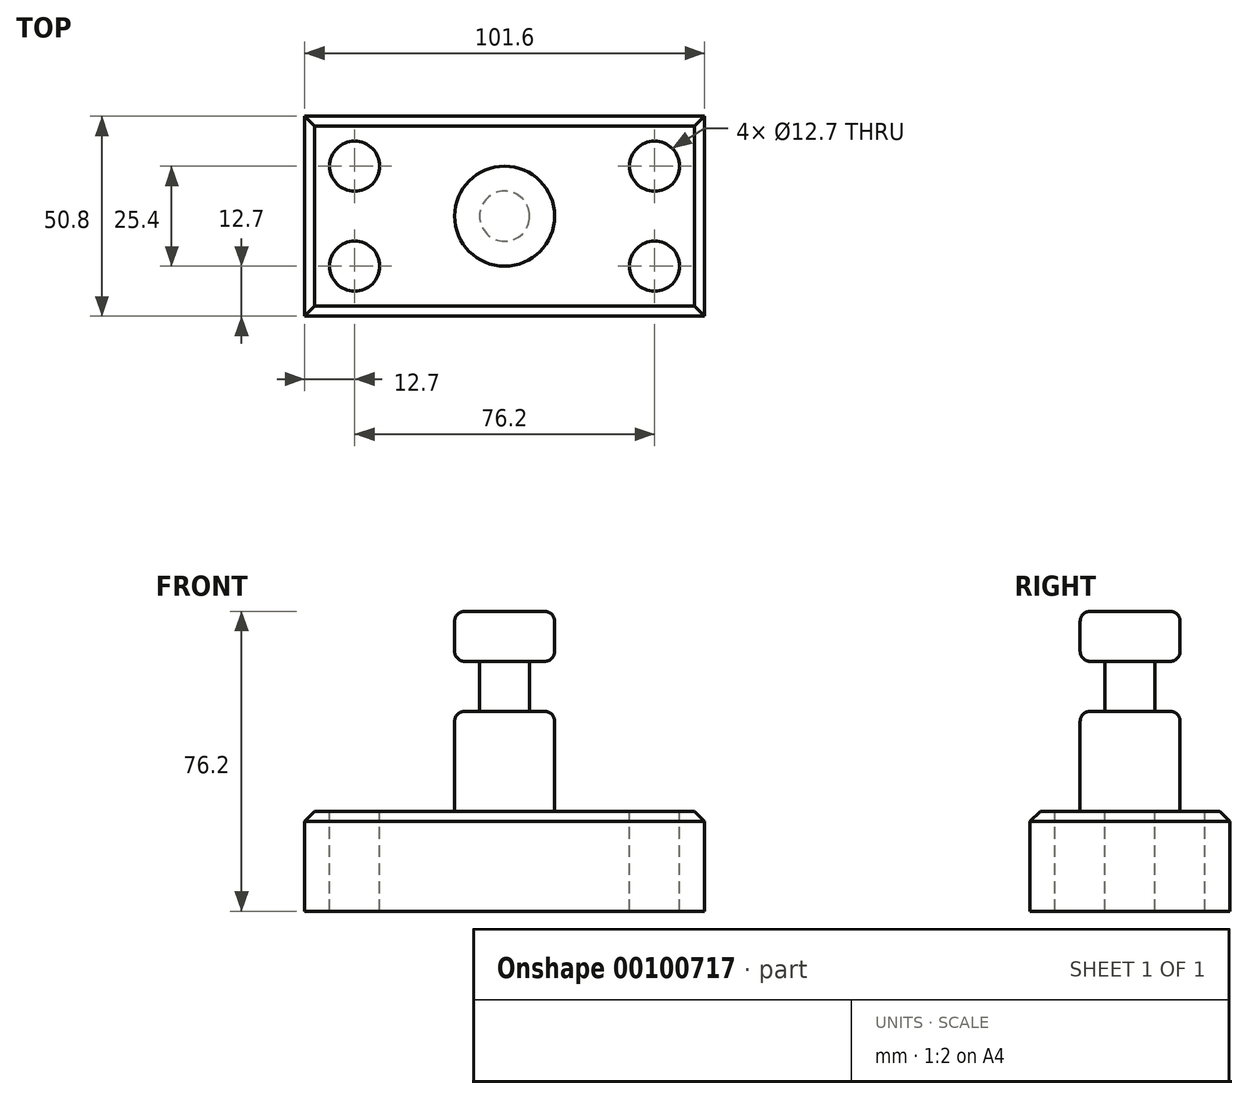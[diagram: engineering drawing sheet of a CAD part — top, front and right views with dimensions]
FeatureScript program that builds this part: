
annotation { "Feature Type Name" : "Feature", "Feature Type Description" : "" }
export const myFeature = defineFeature(function(context is Context, id is Id, definition is map)
    precondition{}
    {
        {
            var Q0;
            Q0=qCreatedBy(makeId("Top.planeOp"),FACE);
            var sketch = newSketch(context, id + "F0", { "sketchPlane" : qUnion([Q0])});
            skLineSegment(sketch, "E0.bottom", {"start": v(-50.8, 25.4) * mm, "end": v(50.8, 25.4) * mm});
            skLineSegment(sketch, "E0.top", {"start": v(-50.8, -25.4) * mm, "end": v(50.8, -25.4) * mm});
            skLineSegment(sketch, "E0.left", {"start": v(-50.8, 25.4) * mm, "end": v(-50.8, -25.4) * mm});
            skLineSegment(sketch, "E0.right", {"start": v(50.8, 25.4) * mm, "end": v(50.8, -25.4) * mm});
            skPoint(sketch, "E0.middle", {"position": v(0, 0) * mm});
            skSolve(sketch);
        }
        {
            var Q0;
            Q0 = qSketchRegion(id + "F0", true);
            extrude(context, id + "F1", {"entities" : qUnion([Q0]), "depth" : 25.4 * mm});
        }
        {
            var Q0;
            Q0=makeQuery(id+"F1.opExtrude","CAP_FACE",FACE,{"disambiguationData":[OSD([sQuery(id+"F0.wireOp",EDGE,"E0.bottom"),sQuery(id+"F0.wireOp",EDGE,"E0.top"),sQuery(id+"F0.wireOp",EDGE,"E0.left"),sQuery(id+"F0.wireOp",EDGE,"E0.right")])],"isStart":false});
            var sketch = newSketch(context, id + "F2", { "sketchPlane" : qUnion([Q0])});
            skCircle(sketch, "E1", {"center": v(-38.1, 12.7) * mm, "radius": 6.35 * mm});
            skCircle(sketch, "E2", {"center": v(38.1, 12.7) * mm, "radius": 6.35 * mm});
            skCircle(sketch, "E3", {"center": v(38.1, -12.7) * mm, "radius": 6.35 * mm});
            skCircle(sketch, "E4", {"center": v(-38.1, -12.7) * mm, "radius": 6.35 * mm});
            skSolve(sketch);
        }
        {
            var Q0;
            Q0=makeQuery(id+"F2.imprint","IMPRINT",FACE,{"disambiguationData":[TD([[makeQuery(id+"F2.imprint","IMPRINT",EDGE,{"derivedFrom":sQuery(id+"F2.wireOp",EDGE,"E2")}),1.0]])]});
            var Q1;
            Q1=makeQuery(id+"F2.imprint","IMPRINT",FACE,{"disambiguationData":[TD([[makeQuery(id+"F2.imprint","IMPRINT",EDGE,{"derivedFrom":sQuery(id+"F2.wireOp",EDGE,"E1")}),1.0]])]});
            var Q2;
            Q2=makeQuery(id+"F2.imprint","IMPRINT",FACE,{"disambiguationData":[TD([[makeQuery(id+"F2.imprint","IMPRINT",EDGE,{"derivedFrom":sQuery(id+"F2.wireOp",EDGE,"E4")}),1.0]])]});
            var Q3;
            Q3=makeQuery(id+"F2.imprint","IMPRINT",FACE,{"disambiguationData":[TD([[makeQuery(id+"F2.imprint","IMPRINT",EDGE,{"derivedFrom":sQuery(id+"F2.wireOp",EDGE,"E3")}),1.0]])]});
            extrude(context, id + "F3", {"entities" : qUnion([Q0, Q1, Q2, Q3]), "operationType" : NewBodyOperationType.REMOVE, "endBound" : BoundingType.THROUGH_ALL, "oppositeDirection" : true, "depth" : 25.4 * mm});
        }
        {
            var Q0;
            Q0=qCreatedBy(makeId("Front.planeOp"),FACE);
            var sketch = newSketch(context, id + "F4", { "sketchPlane" : qUnion([Q0])});
            skLineSegment(sketch, "E5.bottom", {"start": v(0, 25.4) * mm, "end": v(-12.7, 25.4) * mm});
            skLineSegment(sketch, "E5.top", {"start": v(0, 76.2) * mm, "end": v(-12.7, 76.2) * mm});
            skLineSegment(sketch, "E5.left", {"start": v(0, 25.4) * mm, "end": v(0, 76.2) * mm});
            skLineSegment(sketch, "E5.right", {"start": v(-12.7, 25.4) * mm, "end": v(-12.7, 76.2) * mm});
            skSolve(sketch);
        }
        {
            var Q0;
            Q0 = qSketchRegion(id + "F4", true);
            var Q1;
            Q1=sQuery(id+"F4.wireOp",EDGE,"E5.left");
            revolve(context, id + "F5", {"operationType" : NewBodyOperationType.ADD, "entities" : qUnion([Q0]), "axis" : qUnion([Q1]), "revolveType" : RevolveType.FULL});
        }
        {
            var Q0;
            Q0=qCreatedBy(makeId("Front.planeOp"),FACE);
            var sketch = newSketch(context, id + "F6", { "sketchPlane" : qUnion([Q0])});
            skLineSegment(sketch, "E6.bottom", {"start": v(-19.05, 63.5) * mm, "end": v(-6.35, 63.5) * mm});
            skLineSegment(sketch, "E6.top", {"start": v(-19.05, 50.8) * mm, "end": v(-6.35, 50.8) * mm});
            skLineSegment(sketch, "E6.left", {"start": v(-19.05, 63.5) * mm, "end": v(-19.05, 50.8) * mm});
            skLineSegment(sketch, "E6.right", {"start": v(-6.35, 63.5) * mm, "end": v(-6.35, 50.8) * mm});
            skLineSegment(sketch, "E7", {"start": v(0, 0) * mm, "end": v(0, 81.72) * mm, "construction": true});
            skSolve(sketch);
        }
        {
            var Q0;
            Q0=makeQuery(id+"F6.imprint","IMPRINT",FACE,{"disambiguationData":[TD([[makeQuery(id+"F6.imprint","IMPRINT",EDGE,{"derivedFrom":sQuery(id+"F6.wireOp",EDGE,"E6.bottom")}),-1.0]])]});
            var Q1;
            Q1=sQuery(id+"F6.wireOp",EDGE,"E7");
            revolve(context, id + "F7", {"operationType" : NewBodyOperationType.REMOVE, "entities" : qUnion([Q0]), "axis" : qUnion([Q1]), "revolveType" : RevolveType.FULL, "oppositeDirection" : true});
        }
        {
            var Q0;
            Q0=makeQuery(id+"F7.boolean.opBoolean","INTERSECT",EDGE,{"derivedFrom":[makeQuery(id+"F5.opRevolve","SWEPT_FACE",FACE,{"disambiguationData":[OSD([sQuery(id+"F4.wireOp",EDGE,"E5.right")])]}),makeQuery(id+"F7.opRevolve","SWEPT_FACE",FACE,{"disambiguationData":[OSD([sQuery(id+"F6.wireOp",EDGE,"E6.top")])]})]});
            var Q1;
            Q1=makeQuery(id+"F7.boolean.opBoolean","INTERSECT",EDGE,{"derivedFrom":[makeQuery(id+"F5.opRevolve","SWEPT_FACE",FACE,{"disambiguationData":[OSD([sQuery(id+"F4.wireOp",EDGE,"E5.right")])]}),makeQuery(id+"F7.opRevolve","SWEPT_FACE",FACE,{"disambiguationData":[OSD([sQuery(id+"F6.wireOp",EDGE,"E6.bottom")])]})]});
            var Q2;
            Q2=makeQuery(id+"F5.opRevolve","SWEPT_EDGE",EDGE,{"disambiguationData":[OSD([sQuery(id+"F4.wireOp",EDGE,"E5.bottom"),sQuery(id+"F4.wireOp",EDGE,"E5.right")])]});
            var Q3;
            Q3=makeQuery(id+"F5.opRevolve","SWEPT_EDGE",EDGE,{"disambiguationData":[OSD([sQuery(id+"F4.wireOp",EDGE,"E5.top"),sQuery(id+"F4.wireOp",EDGE,"E5.right")])]});
            fillet(context, id + "F8", {"entities" : qUnion([Q0, Q1, Q2, Q3]), "radius" : 2.54 * mm, "tangentPropagation" : true, "allowEdgeOverflow" : false});
        }
        {
            var Q0;
            Q0=makeQuery(id+"F1.opExtrude","CAP_EDGE",EDGE,{"disambiguationData":[OSD([sQuery(id+"F0.wireOp",EDGE,"E0.left")])],"isStart":false});
            var Q1;
            Q1=makeQuery(id+"F1.opExtrude","CAP_EDGE",EDGE,{"disambiguationData":[OSD([sQuery(id+"F0.wireOp",EDGE,"E0.top")])],"isStart":false});
            var Q2;
            Q2=makeQuery(id+"F1.opExtrude","CAP_EDGE",EDGE,{"disambiguationData":[OSD([sQuery(id+"F0.wireOp",EDGE,"E0.bottom")])],"isStart":false});
            var Q3;
            Q3=makeQuery(id+"F1.opExtrude","CAP_EDGE",EDGE,{"disambiguationData":[OSD([sQuery(id+"F0.wireOp",EDGE,"E0.right")])],"isStart":false});
            chamfer(context, id + "F9", {"entities" : qUnion([Q0, Q1, Q2, Q3]), "width" : 2.54 * mm, "tangentPropagation" : true});
        }
    });
